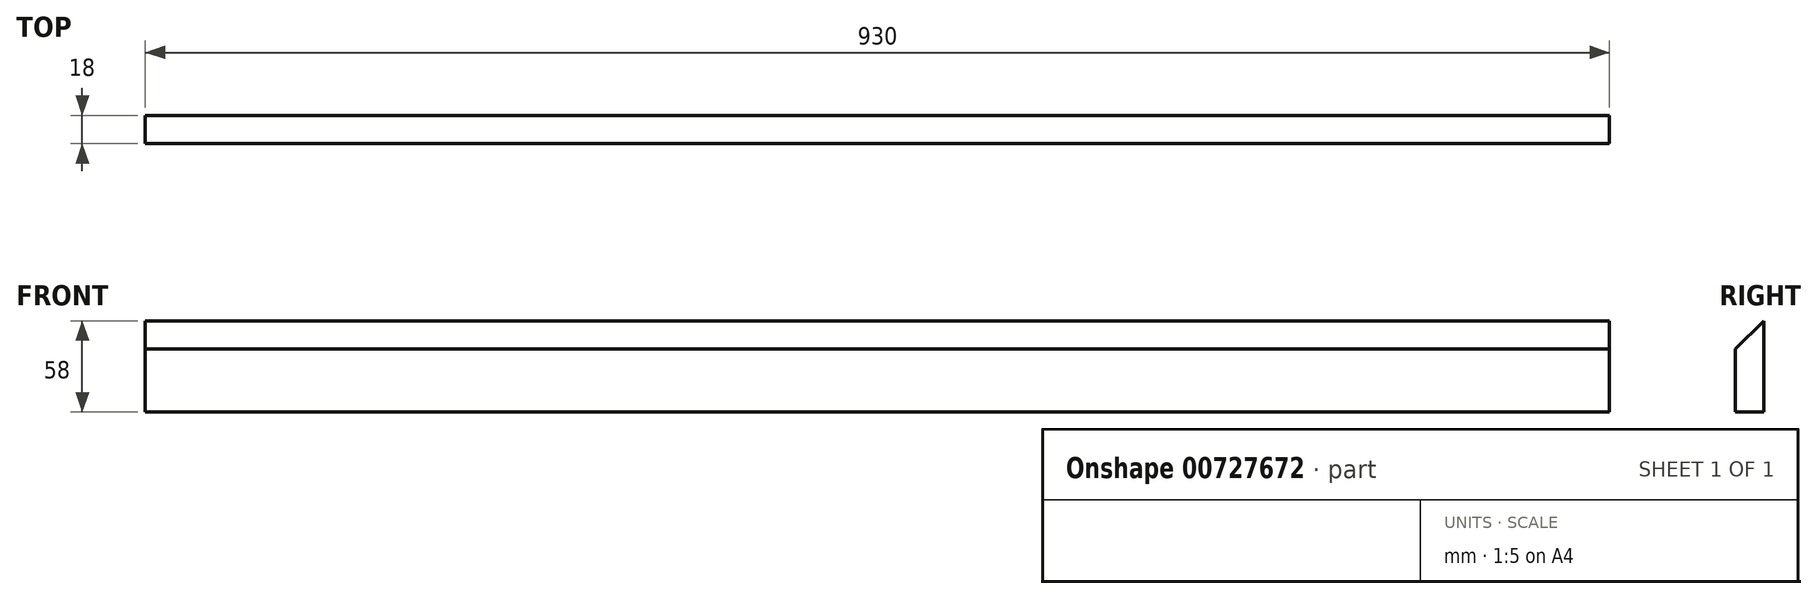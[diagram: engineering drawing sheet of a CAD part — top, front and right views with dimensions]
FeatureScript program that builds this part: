
annotation { "Feature Type Name" : "Feature", "Feature Type Description" : "" }
export const myFeature = defineFeature(function(context is Context, id is Id, definition is map)
    precondition{}
    {
        {
            var Q0;
            Q0=qCreatedBy(makeId("Front.planeOp"),FACE);
            var sketch = newSketch(context, id + "F0", { "sketchPlane" : qUnion([Q0])});
            skLineSegment(sketch, "E0.bottom", {"start": v(-465, -29) * mm, "end": v(465, -29) * mm});
            skLineSegment(sketch, "E0.top", {"start": v(-465, 29) * mm, "end": v(465, 29) * mm});
            skLineSegment(sketch, "E0.left", {"start": v(-465, -29) * mm, "end": v(-465, 29) * mm});
            skLineSegment(sketch, "E0.right", {"start": v(465, -29) * mm, "end": v(465, 29) * mm});
            skPoint(sketch, "E0.middle", {"position": v(0, 0) * mm});
            skSolve(sketch);
        }
        {
            var Q0;
            Q0 = qSketchRegion(id + "F0", true);
            extrude(context, id + "F1", {"entities" : qUnion([Q0]), "depth" : 18 * mm, "offsetDistance" : 25 * mm});
        }
        {
            var Q0;
            Q0=makeQuery(id+"F1.opExtrude","CAP_EDGE",EDGE,{"disambiguationData":[OSD([sQuery(id+"F0.wireOp",EDGE,"E0.top")])],"isStart":false});
            chamfer(context, id + "F2", {"entities" : qUnion([Q0]), "width" : 18 * mm, "tangentPropagation" : true});
        }
    });
